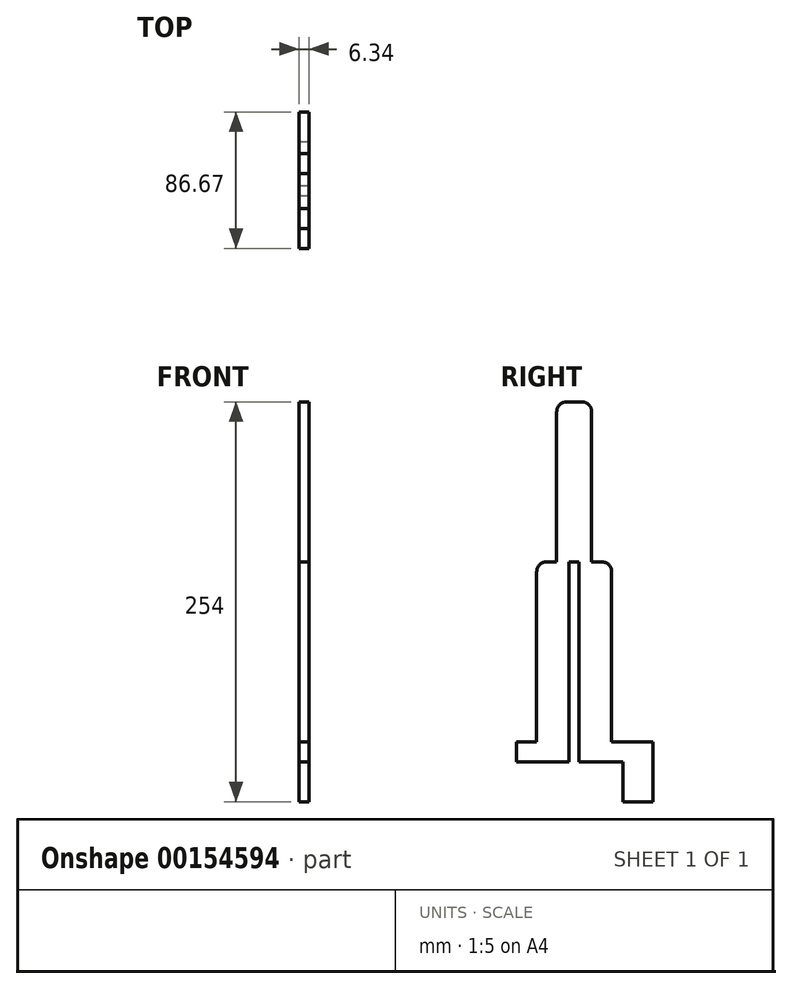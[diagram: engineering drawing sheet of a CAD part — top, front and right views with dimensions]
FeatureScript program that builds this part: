
annotation { "Feature Type Name" : "Feature", "Feature Type Description" : "" }
export const myFeature = defineFeature(function(context is Context, id is Id, definition is map)
    precondition{}
    {
        {
            var Q0;
            Q0=qCreatedBy(makeId("Right.planeOp"),FACE);
            var sketch = newSketch(context, id + "F0", { "sketchPlane" : qUnion([Q0])});
            skLineSegment(sketch, "E0.bottom", {"start": v(23.81, -63.5) * mm, "end": v(3.18, -63.5) * mm});
            skLineSegment(sketch, "E0.top", {"start": v(17.46, 63.5) * mm, "end": v(17.46, 63.5) * mm});
            skLineSegment(sketch, "E0.left", {"start": v(23.81, -63.5) * mm, "end": v(23.81, 57.15) * mm});
            skLineSegment(sketch, "E0.right", {"start": v(-23.81, -63.5) * mm, "end": v(-23.81, 57.15) * mm});
            skPoint(sketch, "E0.middle", {"position": v(0, 0) * mm});
            skLineSegment(sketch, "E1", {"start": v(-11.1, 63.5) * mm, "end": v(-11.1, 158.75) * mm});
            skLineSegment(sketch, "E2", {"start": v(-4.75, 165.1) * mm, "end": v(4.77, 165.1) * mm});
            skLineSegment(sketch, "E3", {"start": v(11.12, 158.75) * mm, "end": v(11.11, 63.5) * mm});
            skLineSegment(sketch, "E4.trimOffspring", {"start": v(-17.45, 63.5) * mm, "end": v(-17.46, 63.5) * mm});
            skPoint(sketch, "E5.start.orphan", {"position": v(0, -63.5) * mm});
            skPoint(sketch, "E6.visualSharp", {"position": v(-11.1, 63.5) * mm});
            skPoint(sketch, "E7.visualSharp", {"position": v(11.11, 63.5) * mm});
            skPoint(sketch, "E8.visualSharp", {"position": v(-23.81, 63.5) * mm});
            skArc(sketch, "E8.filletArc", {"start": v(-17.46, 63.5) * mm, "mid": v(-21.95, 61.64) * mm, "end": v(-23.81, 57.15) * mm});
            skPoint(sketch, "E9.visualSharp", {"position": v(23.81, 63.5) * mm});
            skArc(sketch, "E9.filletArc", {"start": v(23.81, 57.15) * mm, "mid": v(21.95, 61.64) * mm, "end": v(17.46, 63.5) * mm});
            skPoint(sketch, "E10.visualSharp", {"position": v(11.13, 165.1) * mm});
            skArc(sketch, "E10.filletArc", {"start": v(11.12, 158.75) * mm, "mid": v(9.26, 163.24) * mm, "end": v(4.77, 165.1) * mm});
            skPoint(sketch, "E11.visualSharp", {"position": v(-11.1, 165.1) * mm});
            skArc(sketch, "E11.filletArc", {"start": v(-4.75, 165.1) * mm, "mid": v(-9.24, 163.24) * mm, "end": v(-11.1, 158.75) * mm});
            skLineSegment(sketch, "E12", {"start": v(-3.18, -63.5) * mm, "end": v(-3.18, 63.5) * mm});
            skLineSegment(sketch, "E13", {"start": v(-3.18, 63.5) * mm, "end": v(3.17, 63.5) * mm});
            skLineSegment(sketch, "E14", {"start": v(3.17, 63.5) * mm, "end": v(3.17, -63.5) * mm});
            skLineSegment(sketch, "E15.trimOffspring", {"start": v(-3.18, -63.5) * mm, "end": v(-23.81, -63.5) * mm});
            skLineSegment(sketch, "E16", {"start": v(-17.45, 63.5) * mm, "end": v(-11.1, 63.5) * mm});
            skLineSegment(sketch, "E17", {"start": v(11.11, 63.5) * mm, "end": v(17.46, 63.5) * mm});
            skLineSegment(sketch, "E18", {"start": v(3.18, -63.5) * mm, "end": v(31.12, -63.5) * mm});
            skLineSegment(sketch, "E19", {"start": v(31.12, -63.5) * mm, "end": v(31.12, -88.9) * mm});
            skLineSegment(sketch, "E20", {"start": v(31.12, -88.9) * mm, "end": v(50.17, -88.9) * mm});
            skLineSegment(sketch, "E21", {"start": v(50.17, -88.9) * mm, "end": v(50.17, -50.8) * mm});
            skLineSegment(sketch, "E22", {"start": v(50.17, -50.8) * mm, "end": v(23.81, -50.8) * mm});
            skLineSegment(sketch, "E23", {"start": v(23.81, -50.8) * mm, "end": v(23.81, -63.5) * mm});
            skLineSegment(sketch, "E24", {"start": v(-23.81, -63.5) * mm, "end": v(-23.81, -50.82) * mm});
            skLineSegment(sketch, "E25", {"start": v(-23.81, -50.82) * mm, "end": v(-36.51, -50.82) * mm});
            skLineSegment(sketch, "E26", {"start": v(-36.51, -50.82) * mm, "end": v(-36.51, -63.52) * mm});
            skLineSegment(sketch, "E27", {"start": v(-36.51, -63.52) * mm, "end": v(-23.81, -63.5) * mm});
            skSolve(sketch);
        }
        {
            var Q0;
            Q0=qSketchRegion(id+"F0",true);
            extrude(context, id + "F1", {"entities" : qUnion([Q0]), "endBound" : BoundingType.SYMMETRIC, "depth" : 6.35 * mm});
        }
    });
